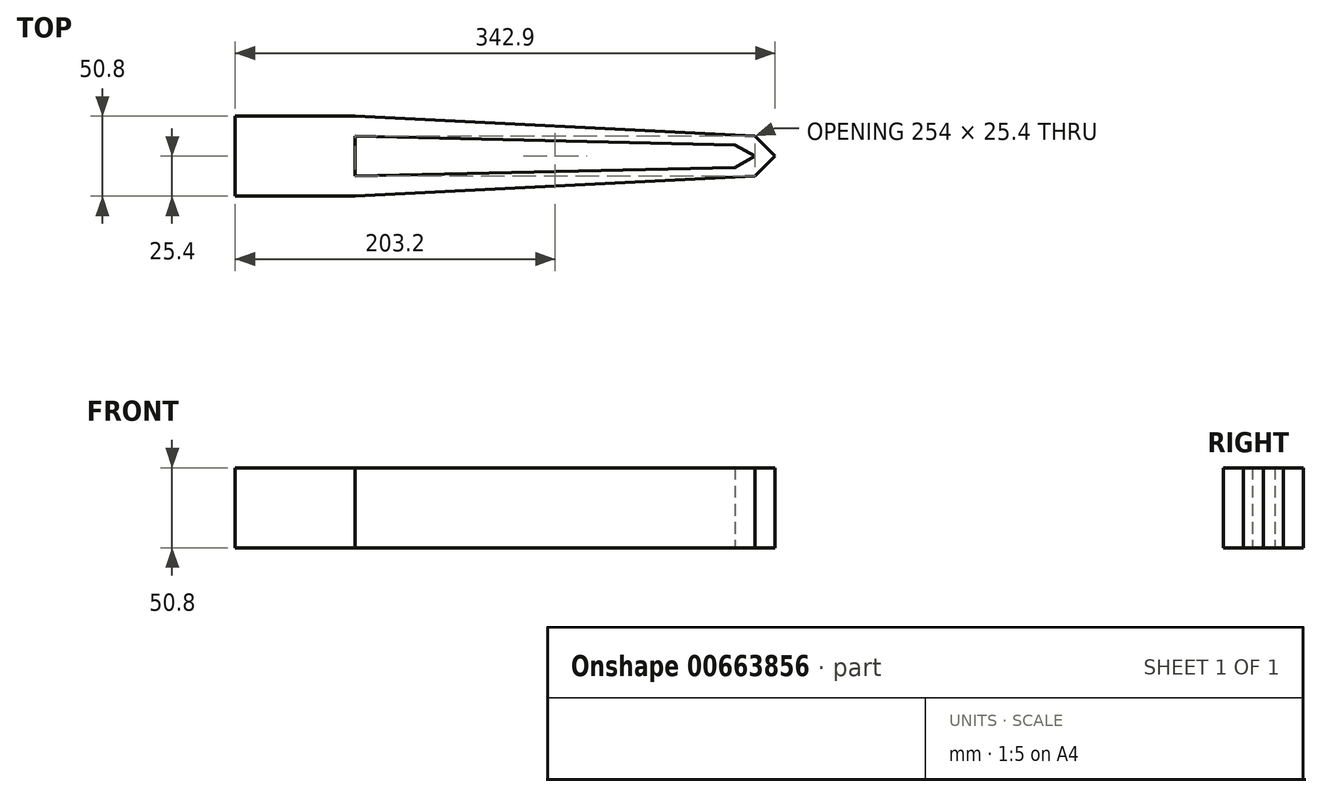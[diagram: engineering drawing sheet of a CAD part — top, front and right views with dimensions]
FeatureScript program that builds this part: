
annotation { "Feature Type Name" : "Feature", "Feature Type Description" : "" }
export const myFeature = defineFeature(function(context is Context, id is Id, definition is map)
    precondition{}
    {
        {
            var Q0;
            Q0=qCreatedBy(makeId("Top.planeOp"),FACE);
            var sketch = newSketch(context, id + "F0", { "sketchPlane" : qUnion([Q0])});
            skLineSegment(sketch, "E0", {"start": v(0, 0) * mm, "end": v(0, 50.8) * mm});
            skLineSegment(sketch, "E1", {"start": v(0, 50.8) * mm, "end": v(76.2, 50.8) * mm});
            skLineSegment(sketch, "E2", {"start": v(0, 0) * mm, "end": v(76.2, 0) * mm});
            skLineSegment(sketch, "E3", {"start": v(76.2, 0) * mm, "end": v(330.2, 12.7) * mm});
            skLineSegment(sketch, "E4", {"start": v(76.2, 50.8) * mm, "end": v(330.2, 38.1) * mm});
            skLineSegment(sketch, "E5", {"start": v(330.2, 12.7) * mm, "end": v(342.9, 25.4) * mm});
            skLineSegment(sketch, "E6", {"start": v(330.2, 38.1) * mm, "end": v(342.9, 25.4) * mm});
            skLineSegment(sketch, "E7", {"start": v(76.2, 38.1) * mm, "end": v(317.43, 32.48) * mm});
            skLineSegment(sketch, "E8", {"start": v(317.43, 32.48) * mm, "end": v(330.2, 25.4) * mm});
            skLineSegment(sketch, "E9", {"start": v(76.2, 12.7) * mm, "end": v(317.43, 18.32) * mm});
            skLineSegment(sketch, "E10", {"start": v(317.43, 18.32) * mm, "end": v(330.2, 25.4) * mm});
            skLineSegment(sketch, "E11", {"start": v(76.2, 38.1) * mm, "end": v(76.2, 12.7) * mm});
            skSolve(sketch);
        }
        {
            var Q0;
            Q0=makeQuery(id+"F0.imprint","IMPRINT",FACE,{"disambiguationData":[TD([[makeQuery(id+"F0.imprint","IMPRINT",EDGE,{"derivedFrom":sQuery(id+"F0.wireOp",EDGE,"E0")}),-1.0]])]});
            extrude(context, id + "F1", {"entities" : qUnion([Q0]), "depth" : 50.8 * mm, "offsetDistance" : 25.4 * mm});
        }
        {
            var Q0;
            Q0=makeQuery(id+"F1.opExtrude","CAP_FACE",FACE,{"disambiguationData":[OSD([sQuery(id+"F0.wireOp",EDGE,"E0"),sQuery(id+"F0.wireOp",EDGE,"E1"),sQuery(id+"F0.wireOp",EDGE,"E2"),sQuery(id+"F0.wireOp",EDGE,"E3"),sQuery(id+"F0.wireOp",EDGE,"E4"),sQuery(id+"F0.wireOp",EDGE,"E5"),sQuery(id+"F0.wireOp",EDGE,"E6"),sQuery(id+"F0.wireOp",EDGE,"E7"),sQuery(id+"F0.wireOp",EDGE,"E8"),sQuery(id+"F0.wireOp",EDGE,"E9"),sQuery(id+"F0.wireOp",EDGE,"E10"),sQuery(id+"F0.wireOp",EDGE,"E11")])],"isStart":false});
            var sketch = newSketch(context, id + "F2", { "sketchPlane" : qUnion([Q0])});
            skLineSegment(sketch, "E12", {"start": v(76.2, 50.8) * mm, "end": v(76.2, 38.1) * mm});
            skLineSegment(sketch, "E13", {"start": v(76.2, 38.1) * mm, "end": v(76.2, 12.7) * mm});
            skLineSegment(sketch, "E14", {"start": v(76.2, 12.7) * mm, "end": v(76.2, 0) * mm});
            skSolve(sketch);
        }
        {
            var Q0;
            Q0=makeQuery(id+"F2.imprint","IMPRINT",FACE,{"disambiguationData":[TD([[makeQuery(id+"F2.imprint","IMPRINT",EDGE,{"derivedFrom":sQuery(id+"F2.wireOp",EDGE,"E12")}),1.0]])]});
            extrude(context, id + "F3", {"entities" : qUnion([Q0]), "operationType" : NewBodyOperationType.ADD, "oppositeDirection" : true, "depth" : 25.4 * mm, "offsetDistance" : 25.4 * mm});
        }
        {
            var Q0;
            Q0=makeQuery(id+"F1.opExtrude","CAP_FACE",FACE,{"disambiguationData":[OSD([sQuery(id+"F0.wireOp",EDGE,"E0"),sQuery(id+"F0.wireOp",EDGE,"E1"),sQuery(id+"F0.wireOp",EDGE,"E2"),sQuery(id+"F0.wireOp",EDGE,"E3"),sQuery(id+"F0.wireOp",EDGE,"E4"),sQuery(id+"F0.wireOp",EDGE,"E5"),sQuery(id+"F0.wireOp",EDGE,"E6"),sQuery(id+"F0.wireOp",EDGE,"E7"),sQuery(id+"F0.wireOp",EDGE,"E8"),sQuery(id+"F0.wireOp",EDGE,"E9"),sQuery(id+"F0.wireOp",EDGE,"E10"),sQuery(id+"F0.wireOp",EDGE,"E11")])],"isStart":false});
            var sketch = newSketch(context, id + "F4", { "sketchPlane" : qUnion([Q0])});
            skLineSegment(sketch, "E15", {"start": v(76.2, 50.8) * mm, "end": v(76.2, 0) * mm});
            skSolve(sketch);
        }
        {
            var Q0;
            {var subQ0=makeQuery(id+"F1.opExtrude","CAP_EDGE",EDGE,{"disambiguationData":[OSD([sQuery(id+"F0.wireOp",EDGE,"E3")])],"isStart":false});Q0=makeQuery(id+"F4.imprint","IMPRINT",FACE,{"disambiguationData":[TD([[makeQuery(id+"F4.imprint","IMPRINT",EDGE,{"derivedFrom":subQ0}),1.0]])]});}
            extrude(context, id + "F5", {"entities" : qUnion([Q0]), "operationType" : NewBodyOperationType.ADD, "oppositeDirection" : true, "depth" : 25.4 * mm, "offsetDistance" : 25.4 * mm});
        }
    });
